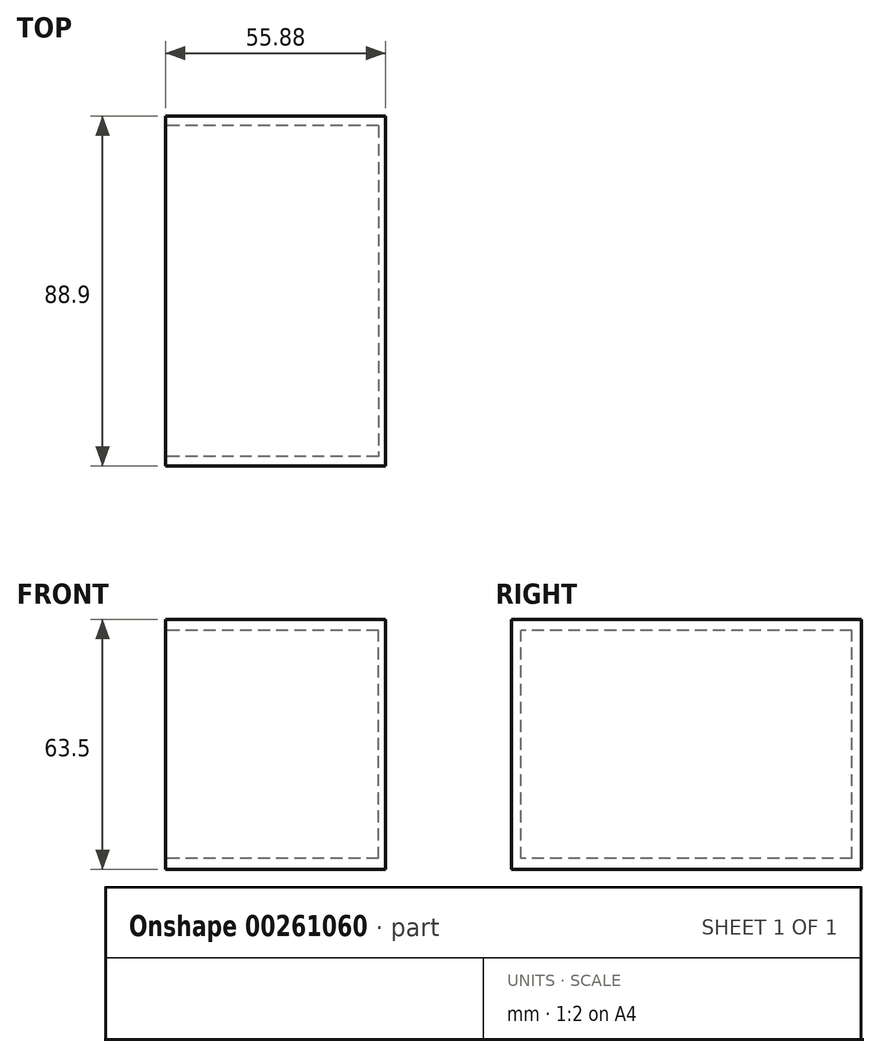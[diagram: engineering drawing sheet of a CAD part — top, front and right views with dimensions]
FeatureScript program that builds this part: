
annotation { "Feature Type Name" : "Feature", "Feature Type Description" : "" }
export const myFeature = defineFeature(function(context is Context, id is Id, definition is map)
    precondition{}
    {
        {
            var Q0;
            Q0=qCreatedBy(makeId("Right.planeOp"),FACE);
            var sketch = newSketch(context, id + "F0", { "sketchPlane" : qUnion([Q0])});
            skLineSegment(sketch, "E0.bottom", {"start": v(44.45, -31.75) * mm, "end": v(-44.45, -31.75) * mm});
            skLineSegment(sketch, "E0.top", {"start": v(44.45, 31.75) * mm, "end": v(-44.45, 31.75) * mm});
            skLineSegment(sketch, "E0.left", {"start": v(44.45, -31.75) * mm, "end": v(44.45, 31.75) * mm});
            skLineSegment(sketch, "E0.right", {"start": v(-44.45, -31.75) * mm, "end": v(-44.45, 31.75) * mm});
            skPoint(sketch, "E0.middle", {"position": v(0, 0) * mm});
            skSolve(sketch);
        }
        {
            var Q0;
            Q0 = qSketchRegion(id + "F0", true);
            extrude(context, id + "F1", {"entities" : qUnion([Q0]), "depth" : 55.88 * mm});
        }
        {
            var Q0;
            Q0=makeQuery(id+"F1.opExtrude","CAP_FACE",FACE,{"disambiguationData":[OSD([sQuery(id+"F0.wireOp",EDGE,"E0.bottom"),sQuery(id+"F0.wireOp",EDGE,"E0.top"),sQuery(id+"F0.wireOp",EDGE,"E0.left"),sQuery(id+"F0.wireOp",EDGE,"E0.right")])],"isStart":true});
            var sketch = newSketch(context, id + "F2", { "sketchPlane" : qUnion([Q0])});
            skLineSegment(sketch, "E1.bottom", {"start": v(-41.98, -28.97) * mm, "end": v(41.98, -28.97) * mm});
            skLineSegment(sketch, "E1.top", {"start": v(-41.98, 28.97) * mm, "end": v(41.98, 28.97) * mm});
            skLineSegment(sketch, "E1.left", {"start": v(-41.98, -28.97) * mm, "end": v(-41.98, 28.97) * mm});
            skLineSegment(sketch, "E1.right", {"start": v(41.98, -28.97) * mm, "end": v(41.98, 28.97) * mm});
            skPoint(sketch, "E1.middle", {"position": v(0, 0) * mm});
            skSolve(sketch);
        }
        {
            var Q0;
            Q0 = qSketchRegion(id + "F2", true);
            extrude(context, id + "F3", {"entities" : qUnion([Q0]), "operationType" : NewBodyOperationType.REMOVE, "oppositeDirection" : true, "depth" : 54.1 * mm});
        }
    });
